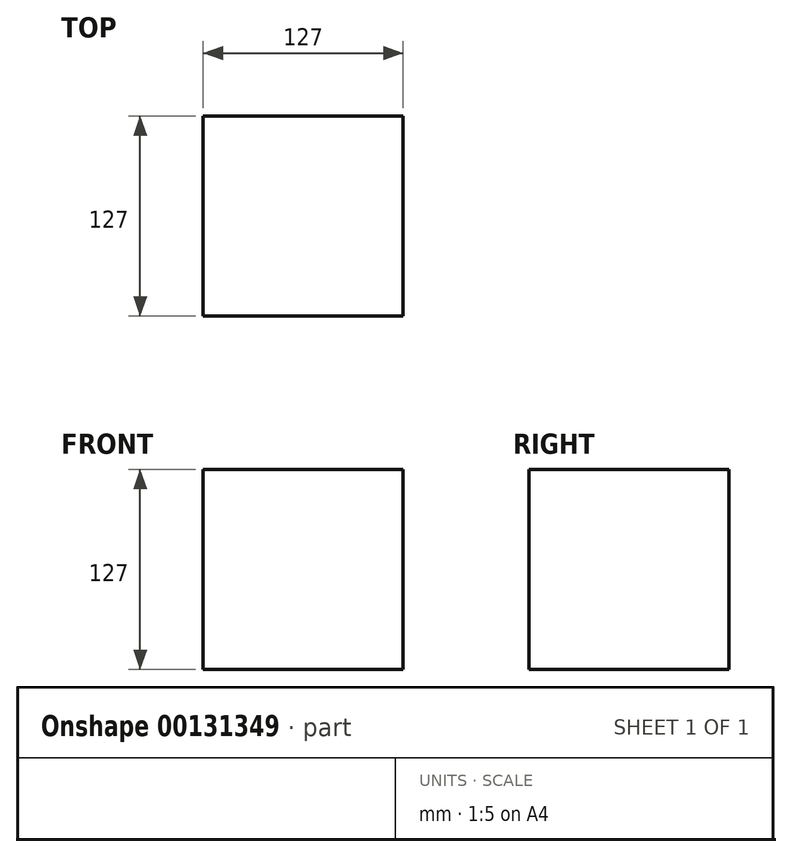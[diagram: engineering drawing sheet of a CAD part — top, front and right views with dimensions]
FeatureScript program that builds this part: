
annotation { "Feature Type Name" : "Feature", "Feature Type Description" : "" }
export const myFeature = defineFeature(function(context is Context, id is Id, definition is map)
    precondition{}
    {
        {
            var Q0;
            Q0=qCreatedBy(makeId("Front.planeOp"),FACE);
            var sketch = newSketch(context, id + "F0", { "sketchPlane" : qUnion([Q0])});
            skLineSegment(sketch, "E0.bottom", {"start": v(-63.5, -63.5) * mm, "end": v(63.5, -63.5) * mm});
            skLineSegment(sketch, "E0.top", {"start": v(-63.5, 63.5) * mm, "end": v(63.5, 63.5) * mm});
            skLineSegment(sketch, "E0.left", {"start": v(-63.5, -63.5) * mm, "end": v(-63.5, 63.5) * mm});
            skLineSegment(sketch, "E0.right", {"start": v(63.5, -63.5) * mm, "end": v(63.5, 63.5) * mm});
            skPoint(sketch, "E0.middle", {"position": v(0, 0) * mm});
            skSolve(sketch);
        }
        {
            var Q0;
            Q0 = qSketchRegion(id + "F0", true);
            extrude(context, id + "F1", {"entities" : qUnion([Q0]), "endBound" : BoundingType.SYMMETRIC, "depth" : 127 * mm});
        }
    });
